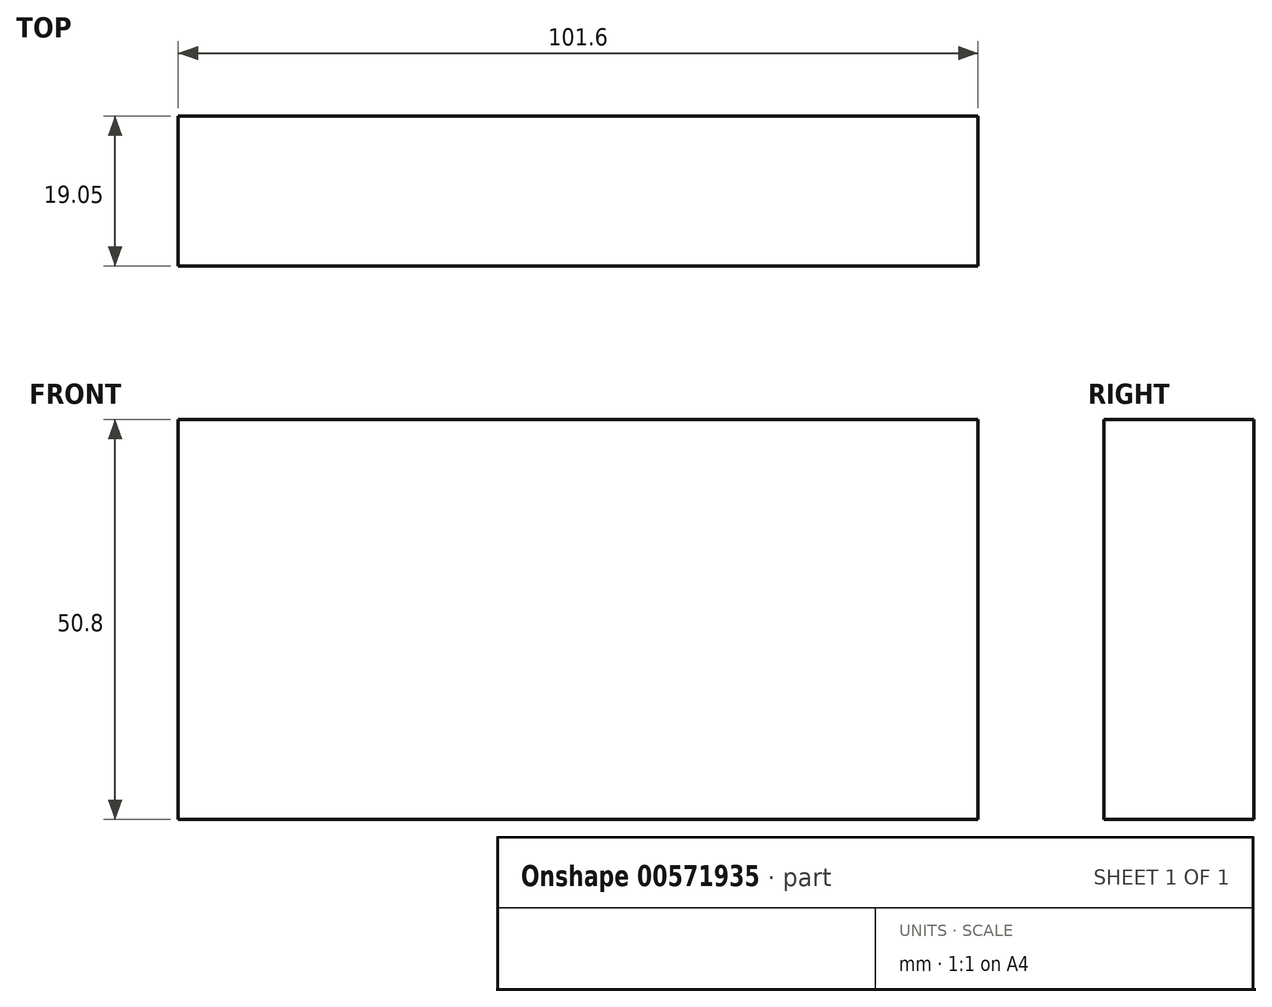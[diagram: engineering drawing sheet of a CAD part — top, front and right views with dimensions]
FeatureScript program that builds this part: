
annotation { "Feature Type Name" : "Feature", "Feature Type Description" : "" }
export const myFeature = defineFeature(function(context is Context, id is Id, definition is map)
    precondition{}
    {
        {
            var Q0;
            Q0=qCreatedBy(makeId("Top.planeOp"),FACE);
            var sketch = newSketch(context, id + "F0", { "sketchPlane" : qUnion([Q0])});
            skLineSegment(sketch, "E0", {"start": v(-74.78, -42.24) * mm, "end": v(26.82, -42.24) * mm});
            skLineSegment(sketch, "E1", {"start": v(26.82, -42.24) * mm, "end": v(26.82, -23.19) * mm});
            skLineSegment(sketch, "E2", {"start": v(26.82, -23.19) * mm, "end": v(-74.78, -23.19) * mm});
            skLineSegment(sketch, "E3", {"start": v(-74.78, -23.19) * mm, "end": v(-74.78, -42.24) * mm});
            skSolve(sketch);
        }
        {
            var Q0;
            Q0 = qSketchRegion(id + "F0", true);
            extrude(context, id + "F1", {"entities" : qUnion([Q0]), "depth" : 50.8 * mm, "offsetDistance" : 25.4 * mm});
        }
    });
